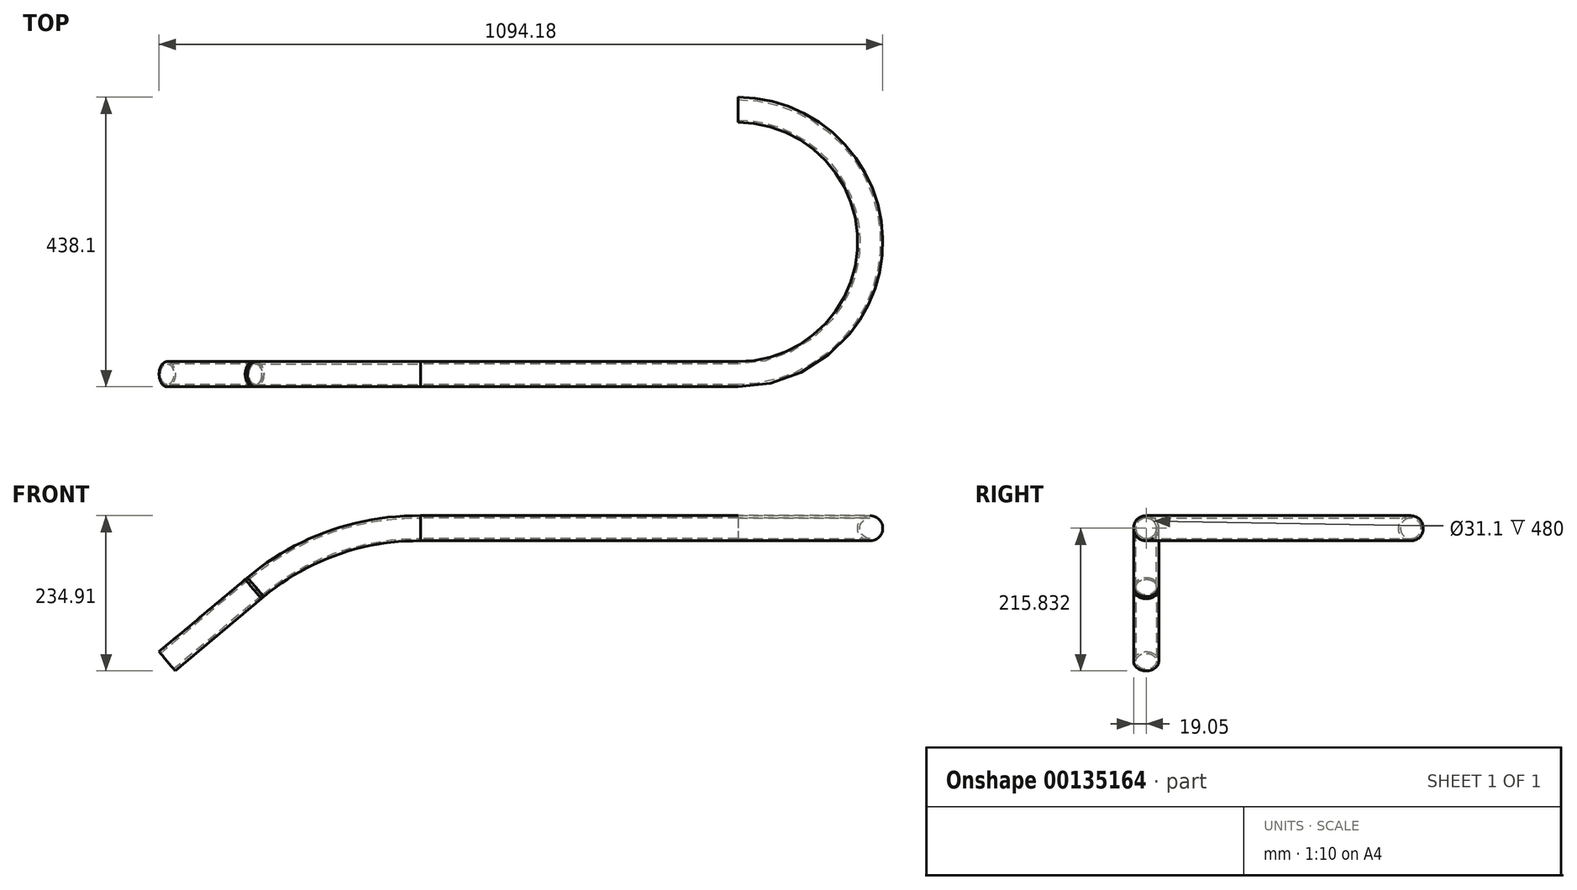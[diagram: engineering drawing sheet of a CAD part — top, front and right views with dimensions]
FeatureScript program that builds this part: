
annotation { "Feature Type Name" : "Feature", "Feature Type Description" : "" }
export const myFeature = defineFeature(function(context is Context, id is Id, definition is map)
    precondition{}
    {
        {
            var Q0;
            Q0=qCreatedBy(makeId("Front.planeOp"),FACE);
            var sketch = newSketch(context, id + "F0", { "sketchPlane" : qUnion([Q0])});
            skPoint(sketch, "E0.orphan", {"position": v(0, 0) * mm});
            skLineSegment(sketch, "E1", {"start": v(0, 25) * mm, "end": v(130.23, 134.27) * mm});
            skLineSegment(sketch, "E2", {"start": v(875.13, 230.7) * mm, "end": v(395.13, 230.7) * mm});
            skPoint(sketch, "E3", {"position": v(395.13, 230.7) * mm});
            skPoint(sketch, "E4", {"position": v(130.23, 134.27) * mm});
            skFitSpline(sketch, "E5", {"points": [v(130.23, 134.27) * mm, v(395.13, 230.7) * mm], "startDerivative": vector(344.72, 289.25) * mm, "endDerivative": vector(450, 0) * mm, "construction": true});
            skLineSegment(sketch, "E6", {"start": v(0, 25) * mm, "end": v(2.25, 22.32) * mm});
            skLineSegment(sketch, "E7.trimOffspring", {"start": v(395.13, 230.7) * mm, "end": v(875.13, 230.7) * mm, "construction": true});
            skLineSegment(sketch, "E8.0", {"start": v(395.13, 211.64) * mm, "end": v(875.13, 211.64) * mm});
            skFitSpline(sketch, "E8.1", {"points": [v(142.47, 119.68) * mm, v(156.84, 131.73) * mm, v(175.62, 147.5) * mm, v(196.54, 164.32) * mm, v(210.5, 174.96) * mm, v(223.05, 183.75) * mm, v(234.55, 190.85) * mm, v(245.37, 196.49) * mm, v(255.98, 200.9) * mm, v(266.94, 204.34) * mm, v(278.85, 206.98) * mm, v(292.22, 208.93) * mm, v(307.5, 210.26) * mm, v(325.03, 211.08) * mm, v(351.87, 211.64) * mm, v(376.38, 211.64) * mm, v(395.13, 211.64) * mm], "construction": true});
            skLineSegment(sketch, "E8.2", {"start": v(12.25, 10.4) * mm, "end": v(142.47, 119.68) * mm});
            skLineSegment(sketch, "E9", {"start": v(395.13, 230.7) * mm, "end": v(395.13, 211.64) * mm});
            skLineSegment(sketch, "E10", {"start": v(875.13, 230.7) * mm, "end": v(875.13, 227.2) * mm});
            skLineSegment(sketch, "E11", {"start": v(130.23, 134.27) * mm, "end": v(142.47, 119.68) * mm});
            skLineSegment(sketch, "E12.0", {"start": v(395.13, 227.2) * mm, "end": v(875.13, 227.2) * mm});
            skFitSpline(sketch, "E12.1", {"points": [v(132.48, 131.6) * mm, v(146.84, 143.65) * mm, v(171.96, 164.72) * mm, v(201.86, 188.34) * mm, v(222.82, 202.28) * mm, v(238.73, 210.57) * mm, v(250.65, 215.53) * mm, v(262.97, 219.4) * mm, v(280.5, 223.27) * mm, v(305.5, 226.06) * mm, v(343.6, 227.2) * mm, v(376.38, 227.2) * mm, v(395.13, 227.2) * mm], "construction": true});
            skLineSegment(sketch, "E12.2", {"start": v(2.25, 22.32) * mm, "end": v(132.48, 131.6) * mm});
            skLineSegment(sketch, "E13", {"start": v(12.25, 10.4) * mm, "end": v(314.13, 10.4) * mm, "construction": true});
            skLineSegment(sketch, "E14", {"start": v(130.23, 134.27) * mm, "end": v(133.6, 137.1) * mm, "construction": true});
            skLineSegment(sketch, "E15", {"start": v(395.13, 230.7) * mm, "end": v(390.72, 230.7) * mm});
            skArc(sketch, "E16.filletArc", {"start": v(390.72, 230.7) * mm, "mid": v(251.84, 205.8) * mm, "end": v(130.24, 134.26) * mm});
            skLineSegment(sketch, "E17", {"start": v(133.6, 137.1) * mm, "end": v(145.85, 122.52) * mm});
            skLineSegment(sketch, "E18", {"start": v(145.85, 122.52) * mm, "end": v(142.47, 119.68) * mm});
            skLineSegment(sketch, "E19", {"start": v(132.48, 131.6) * mm, "end": v(135.86, 134.43) * mm});
            skLineSegment(sketch, "E20", {"start": v(130.24, 134.26) * mm, "end": v(133.6, 137.1) * mm});
            skSolve(sketch);
        }
        {
            var Q0;
            Q0=makeQuery(id+"F0.imprint","IMPRINT",FACE,{"disambiguationData":[TD([[makeQuery(id+"F0.imprint","IMPRINT",EDGE,{"derivedFrom":sQuery(id+"F0.wireOp",EDGE,"E1")}),-1.0]])]});
            var Q1;
            {var subQ0=sQuery(id+"F0.wireOp",EDGE,"E19");Q1=makeQuery(id+"F0.imprint","IMPRINT",FACE,{"disambiguationData":[TD([[makeQuery(id+"F0.imprint","IMPRINT",EDGE,{"derivedFrom":subQ0}),1.0]])]});}
            var Q2;
            Q2=sQuery(id+"F0.wireOp",EDGE,"E8.2");
            revolve(context, id + "F1", {"entities" : qUnion([Q0, Q1]), "axis" : qUnion([Q2]), "revolveType" : RevolveType.FULL});
        }
        {
            var Q0;
            Q0=makeQuery(id+"F0.imprint","IMPRINT",FACE,{"disambiguationData":[TD([[makeQuery(id+"F0.imprint","IMPRINT",EDGE,{"derivedFrom":sQuery(id+"F0.wireOp",EDGE,"E2")}),1.0]])]});
            var Q1;
            Q1=sQuery(id+"F0.wireOp",EDGE,"E8.0");
            revolve(context, id + "F2", {"entities" : qUnion([Q0]), "axis" : qUnion([Q1]), "revolveType" : RevolveType.FULL});
        }
        {
            var Q0;
            Q0=makeQuery(id+"F2.opRevolve","SWEPT_FACE",FACE,{"disambiguationData":[OSD([sQuery(id+"F0.wireOp",EDGE,"E9")])]});
            var Q1;
            Q1=sQuery(id+"F0.wireOp",EDGE,"E16.filletArc");
            sweep(context, id + "F3", {"profiles" : qUnion([Q0]), "path" : qUnion([Q1])});
        }
        {
            var Q0;
            Q0=qCreatedBy(makeId("Top.planeOp"),FACE);
            cPlane(context, id + "F4", {"entities" : qUnion([Q0]), "cplaneType" : CPlaneType.OFFSET, "offset" : 230.7 * mm, "width" : 150 * mm, "height" : 150 * mm});
        }
        {
            var Q0;
            Q0=qCreatedBy(id+"F4.planeOp",FACE);
            var sketch = newSketch(context, id + "F5", { "sketchPlane" : qUnion([Q0])});
            skPoint(sketch, "E21", {"position": v(875.13, 0) * mm});
            skArc(sketch, "E22", {"start": v(875.13, 0) * mm, "mid": v(1075.13, 200) * mm, "end": v(875.13, 400) * mm});
            skLineSegment(sketch, "E23", {"start": v(0, 0) * mm, "end": v(1168.44, 0) * mm, "construction": true});
            skLineSegment(sketch, "E24", {"start": v(875.13, 0) * mm, "end": v(875.13, 19) * mm});
            skArc(sketch, "E25.0", {"start": v(875.13, 19) * mm, "mid": v(1056.13, 200) * mm, "end": v(875.13, 381) * mm});
            skLineSegment(sketch, "E26.trimOffspring", {"start": v(875.13, 381) * mm, "end": v(875.13, 400) * mm});
            skSolve(sketch);
        }
        {
            var Q0;
            Q0=makeQuery(id+"F2.opRevolve","SWEPT_FACE",FACE,{"disambiguationData":[OSD([sQuery(id+"F0.wireOp",EDGE,"E10")])]});
            var Q1;
            Q1=sQuery(id+"F5.wireOp",EDGE,"E22");
            sweep(context, id + "F6", {"operationType" : NewBodyOperationType.ADD, "profiles" : qUnion([Q0]), "path" : qUnion([Q1])});
        }
    });
